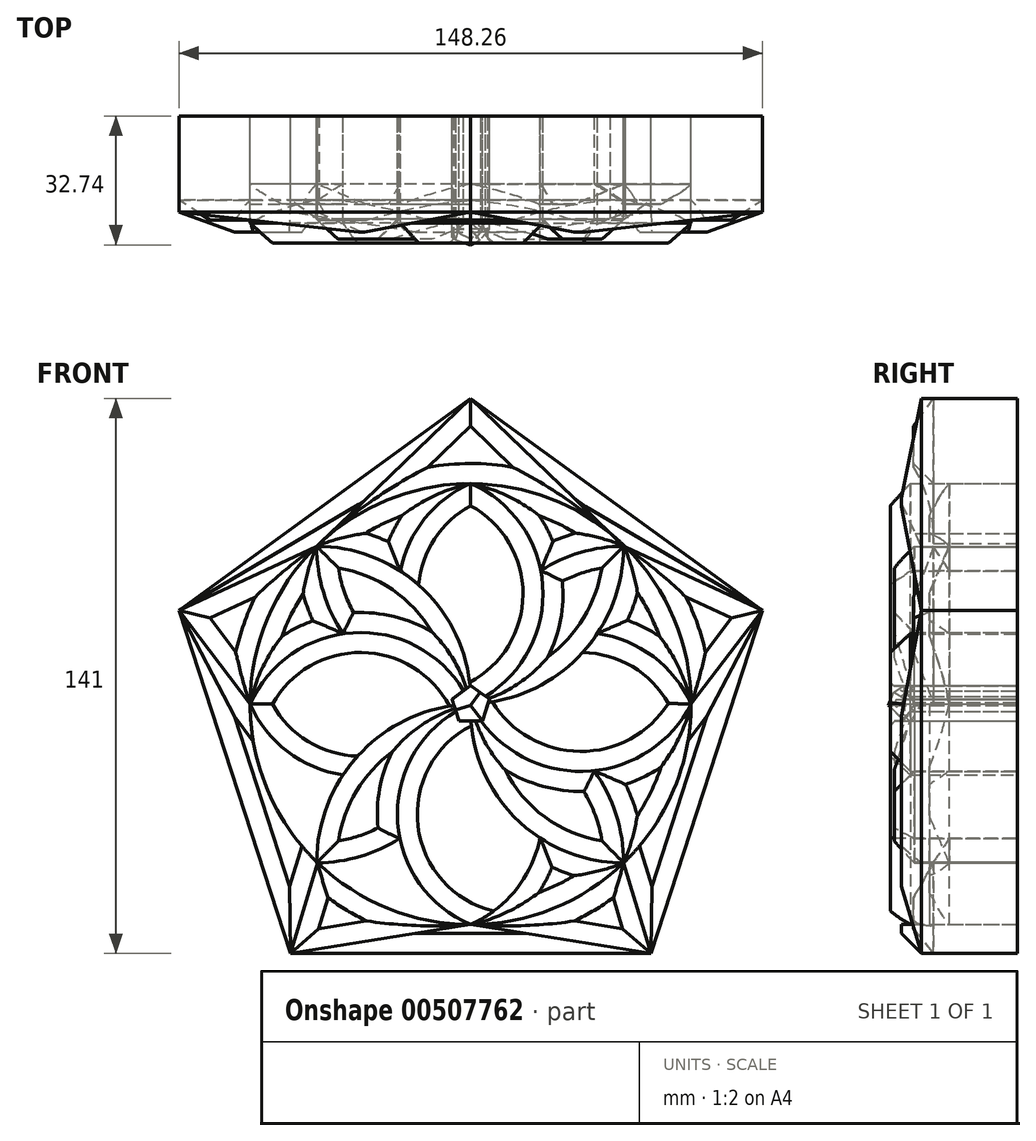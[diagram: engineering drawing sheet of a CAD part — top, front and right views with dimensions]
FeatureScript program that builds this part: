
annotation { "Feature Type Name" : "Feature", "Feature Type Description" : "" }
export const myFeature = defineFeature(function(context is Context, id is Id, definition is map)
    precondition{}
    {
        {
            var Q0;
            Q0=qCreatedBy(makeId("Front.planeOp"),FACE);
            var sketch = newSketch(context, id + "F0", { "sketchPlane" : qUnion([Q0])});
            skCircle(sketch, "E0", {"center": v(0, 0) * mm, "radius": 56.02 * mm});
            skLineSegment(sketch, "E1.top", {"start": v(-39.14, -40.34) * mm, "end": v(-38.88, -40.34) * mm});
            skArc(sketch, "E2", {"start": v(3.77, 1.96) * mm, "mid": v(18.3, 30.13) * mm, "end": v(0, 56.02) * mm});
            skArc(sketch, "E3", {"start": v(0, 56.02) * mm, "mid": v(-11.67, 47.1) * mm, "end": v(-17.83, 33.78) * mm});
            skArc(sketch, "E4", {"start": v(38.88, 40.08) * mm, "mid": v(27.9, 38.5) * mm, "end": v(17.8, 33.88) * mm});
            skArc(sketch, "E5", {"start": v(56.02, 0) * mm, "mid": v(46.42, 12.04) * mm, "end": v(32.18, 17.9) * mm});
            skArc(sketch, "E6", {"start": v(2.69, -4.33) * mm, "mid": v(30.56, -17.02) * mm, "end": v(56.02, 0) * mm});
            skArc(sketch, "E7", {"start": v(4.47, 0.39) * mm, "mid": v(29.08, 13.82) * mm, "end": v(38.88, 40.08) * mm});
            skArc(sketch, "E8", {"start": v(38.88, -40.34) * mm, "mid": v(36.96, -28.05) * mm, "end": v(31.4, -16.94) * mm});
            skArc(sketch, "E9", {"start": v(0.08, -4.34) * mm, "mid": v(12.42, -29.95) * mm, "end": v(38.88, -40.34) * mm});
            skArc(sketch, "E10", {"start": v(-39.14, 40.08) * mm, "mid": v(-37.42, 28.47) * mm, "end": v(-32.41, 17.86) * mm});
            skArc(sketch, "E11", {"start": v(-39.14, -40.34) * mm, "mid": v(-28.13, -38.76) * mm, "end": v(-18, -34.15) * mm});
            skArc(sketch, "E12", {"start": v(-4.22, -0.35) * mm, "mid": v(-29.18, -13.8) * mm, "end": v(-39.14, -40.34) * mm});
            skArc(sketch, "E13", {"start": v(0, -56.02) * mm, "mid": v(11.5, -47.18) * mm, "end": v(17.64, -34.03) * mm});
            skArc(sketch, "E14", {"start": v(-3.71, -1.86) * mm, "mid": v(-18.56, -30.09) * mm, "end": v(0, -56.02) * mm});
            skArc(sketch, "E15", {"start": v(-56.02, 0) * mm, "mid": v(-46.54, -12.06) * mm, "end": v(-32.4, -18) * mm});
            skArc(sketch, "E16", {"start": v(-1.77, 3.4) * mm, "mid": v(-29.92, 18.12) * mm, "end": v(-56.02, 0) * mm});
            skLineSegment(sketch, "E17.trimOffspring", {"start": v(-39.14, -40.08) * mm, "end": v(-39.14, -40.34) * mm});
            skArc(sketch, "E18.trimOffspring", {"start": v(0, -0.3) * mm, "mid": v(0, -0.15) * mm, "end": v(0, 0) * mm});
            skPoint(sketch, "E19.cCircle.perimeterSnap0", {"position": v(0.02, -1.3) * mm});
            skLineSegment(sketch, "E19.0", {"start": v(2.95, -4.33) * mm, "end": v(-2.91, -4.35) * mm});
            skLineSegment(sketch, "E19.1", {"start": v(-2.91, -4.35) * mm, "end": v(-4.74, 1.23) * mm});
            skLineSegment(sketch, "E19.2", {"start": v(-4.74, 1.23) * mm, "end": v(0, 4.68) * mm});
            skLineSegment(sketch, "E19.3", {"start": v(0, 4.68) * mm, "end": v(4.75, 1.25) * mm});
            skLineSegment(sketch, "E19.4", {"start": v(4.75, 1.25) * mm, "end": v(2.95, -4.33) * mm});
            skPoint(sketch, "E19.0.midPoint", {"position": v(0.02, -4.34) * mm});
            skPoint(sketch, "E19.0.midPoint.positionSnap0", {"position": v(0.02, -1.3) * mm});
            skArc(sketch, "E20.trimOffspring", {"start": v(-0.16, 4.57) * mm, "mid": v(-12.77, 29.87) * mm, "end": v(-39.14, 40.08) * mm});
            skArc(sketch, "E21.trimOffspring", {"start": v(-3.83, -1.56) * mm, "mid": v(-3.77, -1.71) * mm, "end": v(-3.71, -1.86) * mm, "construction": true});
            skArc(sketch, "E22.trimOffspring", {"start": v(0.02, -4.34) * mm, "mid": v(0.05, -4.34) * mm, "end": v(0.08, -4.34) * mm, "construction": true});
            skLineSegment(sketch, "E23.0", {"start": v(45.82, -63.36) * mm, "end": v(-45.8, -63.36) * mm});
            skLineSegment(sketch, "E23.1", {"start": v(-45.8, -63.36) * mm, "end": v(-74.12, 23.78) * mm});
            skLineSegment(sketch, "E23.2", {"start": v(-74.12, 23.78) * mm, "end": v(0, 77.64) * mm});
            skLineSegment(sketch, "E23.3", {"start": v(0, 77.64) * mm, "end": v(74.14, 23.78) * mm});
            skLineSegment(sketch, "E23.4", {"start": v(74.14, 23.78) * mm, "end": v(45.82, -63.36) * mm});
            skPoint(sketch, "E23.0.midPoint", {"position": v(0, -63.36) * mm});
            skLineSegment(sketch, "E24", {"start": v(-74.12, 23.78) * mm, "end": v(-56.02, 0) * mm});
            skLineSegment(sketch, "E25", {"start": v(-74.12, 23.78) * mm, "end": v(-39.14, 40.08) * mm});
            skLineSegment(sketch, "E26", {"start": v(0, 77.64) * mm, "end": v(-39.14, 40.08) * mm});
            skLineSegment(sketch, "E27", {"start": v(0, 77.64) * mm, "end": v(38.88, 40.08) * mm});
            skLineSegment(sketch, "E28", {"start": v(74.14, 23.78) * mm, "end": v(38.88, 40.08) * mm});
            skLineSegment(sketch, "E29", {"start": v(74.14, 23.78) * mm, "end": v(56.02, 0) * mm});
            skLineSegment(sketch, "E30", {"start": v(45.82, -63.36) * mm, "end": v(38.88, -40.34) * mm});
            skLineSegment(sketch, "E31", {"start": v(45.82, -63.36) * mm, "end": v(0, -56.02) * mm});
            skLineSegment(sketch, "E32", {"start": v(-45.8, -63.36) * mm, "end": v(-38.88, -40.34) * mm});
            skLineSegment(sketch, "E33", {"start": v(-45.8, -63.36) * mm, "end": v(0, -56.02) * mm});
            skSolve(sketch);
        }
        {
            var Q0;
            Q0=makeQuery(id+"F0.imprint","IMPRINT",FACE,{"disambiguationData":[TD([[makeQuery(id+"F0.imprint","IMPRINT",EDGE,{"derivedFrom":sQuery(id+"F0.wireOp",EDGE,"E1.top")}),-1.0]])]});
            var Q1;
            {var subQ4=sQuery(id+"F0.wireOp",EDGE,"E23.2");Q1=makeQuery(id+"F0.imprint","IMPRINT",FACE,{"disambiguationData":[TD([[makeQuery(id+"F0.imprint","IMPRINT",EDGE,{"derivedFrom":subQ4}),-1.0]])]});}
            var Q2;
            {var subQ5=sQuery(id+"F0.wireOp",EDGE,"E23.3");Q2=makeQuery(id+"F0.imprint","IMPRINT",FACE,{"disambiguationData":[TD([[makeQuery(id+"F0.imprint","IMPRINT",EDGE,{"derivedFrom":subQ5}),-1.0]])]});}
            var Q3;
            Q3=makeQuery(id+"F0.imprint","IMPRINT",FACE,{"disambiguationData":[TD([[makeQuery(id+"F0.imprint","IMPRINT",EDGE,{"derivedFrom":sQuery(id+"F0.wireOp",EDGE,"E23.0")}),-1.0]])]});
            var Q4;
            Q4=makeQuery(id+"F0.imprint","IMPRINT",FACE,{"disambiguationData":[TD([[makeQuery(id+"F0.imprint","IMPRINT",EDGE,{"derivedFrom":sQuery(id+"F0.wireOp",EDGE,"E23.4")}),-1.0]])]});
            extrude(context, id + "F1", {"entities" : qUnion([Q0, Q1, Q2, Q3, Q4]), "depth" : 29.46 * mm});
        }
        {
            var Q0;
            {var subQ0=sQuery(id+"F0.wireOp",EDGE,"E0");var subQ2=sQuery(id+"F0.wireOp",EDGE,"E27");var subQ3=makeQuery(id+"F0.imprint","INTERSECT",VERTEX,{"derivedFrom":[subQ0,subQ2]});Q0=makeQuery(id+"F0.imprint","IMPRINT",FACE,{"disambiguationData":[TD([[makeQuery(id+"F0.imprint","IMPRINT",EDGE,{"disambiguationData":[TD([[subQ3,-1.0]])],"derivedFrom":subQ0}),-1.0]])]});}
            var Q1;
            {var subQ2=sQuery(id+"F0.wireOp",EDGE,"E24");Q1=makeQuery(id+"F0.imprint","IMPRINT",FACE,{"disambiguationData":[TD([[makeQuery(id+"F0.imprint","IMPRINT",EDGE,{"derivedFrom":subQ2}),1.0]])]});}
            var Q2;
            {var subQ0=sQuery(id+"F0.wireOp",EDGE,"E32");Q2=makeQuery(id+"F0.imprint","IMPRINT",FACE,{"disambiguationData":[TD([[makeQuery(id+"F0.imprint","IMPRINT",EDGE,{"derivedFrom":subQ0}),-1.0]])]});}
            var Q3;
            {var subQ0=sQuery(id+"F0.wireOp",EDGE,"E30");Q3=makeQuery(id+"F0.imprint","IMPRINT",FACE,{"disambiguationData":[TD([[makeQuery(id+"F0.imprint","IMPRINT",EDGE,{"derivedFrom":subQ0}),1.0]])]});}
            var Q4;
            {var subQ0=sQuery(id+"F0.wireOp",EDGE,"E29");Q4=makeQuery(id+"F0.imprint","IMPRINT",FACE,{"disambiguationData":[TD([[makeQuery(id+"F0.imprint","IMPRINT",EDGE,{"derivedFrom":subQ0}),-1.0]])]});}
            extrude(context, id + "F2", {"entities" : qUnion([Q0, Q1, Q2, Q3, Q4]), "depth" : 26.42 * mm});
        }
        {
            var Q0;
            {var subQ0=sQuery(id+"F0.wireOp",EDGE,"E3");Q0=makeQuery(id+"F0.imprint","IMPRINT",FACE,{"disambiguationData":[TD([[makeQuery(id+"F0.imprint","IMPRINT",EDGE,{"derivedFrom":subQ0}),-1.0]])]});}
            var Q1;
            {var subQ0=sQuery(id+"F0.wireOp",EDGE,"E10");Q1=makeQuery(id+"F0.imprint","IMPRINT",FACE,{"disambiguationData":[TD([[makeQuery(id+"F0.imprint","IMPRINT",EDGE,{"derivedFrom":subQ0}),-1.0]])]});}
            var Q2;
            {var subQ0=sQuery(id+"F0.wireOp",EDGE,"E15");Q2=makeQuery(id+"F0.imprint","IMPRINT",FACE,{"disambiguationData":[TD([[makeQuery(id+"F0.imprint","IMPRINT",EDGE,{"derivedFrom":subQ0}),-1.0]])]});}
            var Q3;
            {var subQ2=sQuery(id+"F0.wireOp",EDGE,"E11");var subQ4=sQuery(id+"F0.wireOp",EDGE,"E14");var subQ5=makeQuery(id+"F0.imprint","INTERSECT",VERTEX,{"derivedFrom":[subQ2,subQ4]});Q3=makeQuery(id+"F0.imprint","IMPRINT",FACE,{"disambiguationData":[TD([[makeQuery(id+"F0.imprint","IMPRINT",EDGE,{"disambiguationData":[TD([[subQ5,1.0]])],"derivedFrom":subQ2}),-1.0]])]});}
            var Q4;
            {var subQ3=sQuery(id+"F0.wireOp",EDGE,"E13");Q4=makeQuery(id+"F0.imprint","IMPRINT",FACE,{"disambiguationData":[TD([[makeQuery(id+"F0.imprint","IMPRINT",EDGE,{"derivedFrom":subQ3}),-1.0]])]});}
            var Q5;
            {var subQ3=sQuery(id+"F0.wireOp",EDGE,"E8");Q5=makeQuery(id+"F0.imprint","IMPRINT",FACE,{"disambiguationData":[TD([[makeQuery(id+"F0.imprint","IMPRINT",EDGE,{"derivedFrom":subQ3}),-1.0]])]});}
            var Q6;
            {var subQ0=sQuery(id+"F0.wireOp",EDGE,"E5");Q6=makeQuery(id+"F0.imprint","IMPRINT",FACE,{"disambiguationData":[TD([[makeQuery(id+"F0.imprint","IMPRINT",EDGE,{"derivedFrom":subQ0}),-1.0]])]});}
            var Q7;
            {var subQ5=sQuery(id+"F0.wireOp",EDGE,"E4");Q7=makeQuery(id+"F0.imprint","IMPRINT",FACE,{"disambiguationData":[TD([[makeQuery(id+"F0.imprint","IMPRINT",EDGE,{"derivedFrom":subQ5}),-1.0]])]});}
            extrude(context, id + "F3", {"entities" : qUnion([Q0, Q1, Q2, Q3, Q4, Q5, Q6, Q7]), "depth" : 22.35 * mm});
        }
        {
            var Q0;
            {var subQ8=sQuery(id+"F0.wireOp",EDGE,"E3");Q0=makeQuery(id+"F0.imprint","IMPRINT",FACE,{"disambiguationData":[TD([[makeQuery(id+"F0.imprint","IMPRINT",EDGE,{"derivedFrom":subQ8}),1.0]])]});}
            var Q1;
            {var subQ4=sQuery(id+"F0.wireOp",EDGE,"E13");Q1=makeQuery(id+"F0.imprint","IMPRINT",FACE,{"disambiguationData":[TD([[makeQuery(id+"F0.imprint","IMPRINT",EDGE,{"derivedFrom":subQ4}),1.0]])]});}
            var Q2;
            {var subQ1=sQuery(id+"F0.wireOp",EDGE,"E5");Q2=makeQuery(id+"F0.imprint","IMPRINT",FACE,{"disambiguationData":[TD([[makeQuery(id+"F0.imprint","IMPRINT",EDGE,{"derivedFrom":subQ1}),1.0]])]});}
            var Q3;
            {var subQ2=sQuery(id+"F0.wireOp",EDGE,"E15");Q3=makeQuery(id+"F0.imprint","IMPRINT",FACE,{"disambiguationData":[TD([[makeQuery(id+"F0.imprint","IMPRINT",EDGE,{"derivedFrom":subQ2}),1.0]])]});}
            extrude(context, id + "F4", {"entities" : qUnion([Q0, Q1, Q2, Q3]), "depth" : 32.26 * mm});
        }
        {
            var Q0;
            {var subQ6=sQuery(id+"F0.wireOp",EDGE,"E10");Q0=makeQuery(id+"F0.imprint","IMPRINT",FACE,{"disambiguationData":[TD([[makeQuery(id+"F0.imprint","IMPRINT",EDGE,{"derivedFrom":subQ6}),1.0]])]});}
            var Q1;
            {var subQ0=sQuery(id+"F0.wireOp",EDGE,"E12");var subQ2=sQuery(id+"F0.wireOp",EDGE,"E0");var subQ3=makeQuery(id+"F0.imprint","INTERSECT",VERTEX,{"derivedFrom":[subQ2,subQ0]});Q1=makeQuery(id+"F0.imprint","IMPRINT",FACE,{"disambiguationData":[TD([[makeQuery(id+"F0.imprint","IMPRINT",EDGE,{"disambiguationData":[TD([[subQ3,-1.0]])],"derivedFrom":subQ2}),1.0]])]});}
            var Q2;
            {var subQ1=sQuery(id+"F0.wireOp",EDGE,"E8");Q2=makeQuery(id+"F0.imprint","IMPRINT",FACE,{"disambiguationData":[TD([[makeQuery(id+"F0.imprint","IMPRINT",EDGE,{"derivedFrom":subQ1}),1.0]])]});}
            var Q3;
            {var subQ4=sQuery(id+"F0.wireOp",EDGE,"E4");Q3=makeQuery(id+"F0.imprint","IMPRINT",FACE,{"disambiguationData":[TD([[makeQuery(id+"F0.imprint","IMPRINT",EDGE,{"derivedFrom":subQ4}),1.0]])]});}
            extrude(context, id + "F5", {"entities" : qUnion([Q0, Q1, Q2, Q3]), "depth" : 31.24 * mm});
        }
        {
            var Q0;
            {var subQ10=sQuery(id+"F0.wireOp",EDGE,"E19.0");var subQ11=makeQuery(id+"F0.imprint","INTERSECT",VERTEX,{"derivedFrom":[sQuery(id+"F0.wireOp",EDGE,"E6"),subQ10]});Q0=makeQuery(id+"F0.imprint","IMPRINT",FACE,{"disambiguationData":[TD([[makeQuery(id+"F0.imprint","IMPRINT",EDGE,{"disambiguationData":[TD([[subQ11,1.0]])],"derivedFrom":subQ10}),-1.0]])]});}
            extrude(context, id + "F6", {"entities" : qUnion([Q0]), "depth" : 33.78 * mm});
        }
        {
            var Q0;
            Q0=makeQuery(id+"F1.opExtrude","CAP_EDGE",EDGE,{"disambiguationData":[OSD([sQuery(id+"F0.wireOp",EDGE,"E23.3")])],"isStart":false});
            var Q1;
            Q1=makeQuery(id+"F1.opExtrude","CAP_EDGE",EDGE,{"disambiguationData":[OSD([sQuery(id+"F0.wireOp",EDGE,"E23.0")])],"isStart":false});
            var Q2;
            Q2=makeQuery(id+"F1.opExtrude","CAP_EDGE",EDGE,{"disambiguationData":[OSD([sQuery(id+"F0.wireOp",EDGE,"E23.4")])],"isStart":false});
            var Q3;
            Q3=makeQuery(id+"F1.opExtrude","CAP_EDGE",EDGE,{"disambiguationData":[OSD([sQuery(id+"F0.wireOp",EDGE,"E23.1")])],"isStart":false});
            var Q4;
            Q4=makeQuery(id+"F1.opExtrude","CAP_EDGE",EDGE,{"disambiguationData":[OSD([sQuery(id+"F0.wireOp",EDGE,"E32")])],"isStart":false});
            var Q5;
            Q5=makeQuery(id+"F1.opExtrude","CAP_EDGE",EDGE,{"disambiguationData":[OSD([sQuery(id+"F0.wireOp",EDGE,"E24")])],"isStart":false});
            var Q6;
            Q6=makeQuery(id+"F1.opExtrude","CAP_EDGE",EDGE,{"disambiguationData":[OSD([sQuery(id+"F0.wireOp",EDGE,"E23.2")])],"isStart":false});
            var Q7;
            Q7=makeQuery(id+"F1.opExtrude","CAP_EDGE",EDGE,{"disambiguationData":[OSD([sQuery(id+"F0.wireOp",EDGE,"E25")])],"isStart":false});
            var Q8;
            Q8=makeQuery(id+"F1.opExtrude","CAP_EDGE",EDGE,{"disambiguationData":[OSD([sQuery(id+"F0.wireOp",EDGE,"E30")])],"isStart":false});
            var Q9;
            Q9=makeQuery(id+"F1.opExtrude","CAP_EDGE",EDGE,{"disambiguationData":[OSD([sQuery(id+"F0.wireOp",EDGE,"E29")])],"isStart":false});
            var Q10;
            Q10=makeQuery(id+"F1.opExtrude","CAP_EDGE",EDGE,{"disambiguationData":[OSD([sQuery(id+"F0.wireOp",EDGE,"E28")])],"isStart":false});
            chamfer(context, id + "F7", {"entities" : qUnion([Q0, Q1, Q2, Q3, Q4, Q5, Q6, Q7, Q8, Q9, Q10]), "width" : 5.08 * mm, "tangentPropagation" : true});
        }
        {
            var Q0;
            Q0=makeQuery(id+"F2.opExtrude","CAP_FACE",FACE,{"disambiguationData":[OSD([sQuery(id+"F0.wireOp",EDGE,"E0"),sQuery(id+"F0.wireOp",EDGE,"E24"),sQuery(id+"F0.wireOp",EDGE,"E25")])],"isStart":false});
            var Q1;
            Q1=makeQuery(id+"F2.opExtrude","CAP_FACE",FACE,{"disambiguationData":[OSD([sQuery(id+"F0.wireOp",EDGE,"E0"),sQuery(id+"F0.wireOp",EDGE,"E26"),sQuery(id+"F0.wireOp",EDGE,"E27")])],"isStart":false});
            var Q2;
            Q2=makeQuery(id+"F2.opExtrude","CAP_FACE",FACE,{"disambiguationData":[OSD([sQuery(id+"F0.wireOp",EDGE,"E0"),sQuery(id+"F0.wireOp",EDGE,"E28"),sQuery(id+"F0.wireOp",EDGE,"E29")])],"isStart":false});
            var Q3;
            Q3=makeQuery(id+"F2.opExtrude","CAP_FACE",FACE,{"disambiguationData":[OSD([sQuery(id+"F0.wireOp",EDGE,"E0"),sQuery(id+"F0.wireOp",EDGE,"E30"),sQuery(id+"F0.wireOp",EDGE,"E31")])],"isStart":false});
            var Q4;
            Q4=makeQuery(id+"F2.opExtrude","CAP_FACE",FACE,{"disambiguationData":[OSD([sQuery(id+"F0.wireOp",EDGE,"E0"),sQuery(id+"F0.wireOp",EDGE,"E32"),sQuery(id+"F0.wireOp",EDGE,"E33")])],"isStart":false});
            var Q5;
            Q5=makeQuery(id+"F5.opExtrude","CAP_FACE",FACE,{"disambiguationData":[OSD([sQuery(id+"F0.wireOp",EDGE,"E10"),sQuery(id+"F0.wireOp",EDGE,"E16"),sQuery(id+"F0.wireOp",EDGE,"E19.2"),sQuery(id+"F0.wireOp",EDGE,"E20.trimOffspring")])],"isStart":false});
            var Q6;
            Q6=makeQuery(id+"F5.opExtrude","CAP_FACE",FACE,{"disambiguationData":[OSD([sQuery(id+"F0.wireOp",EDGE,"E2"),sQuery(id+"F0.wireOp",EDGE,"E4"),sQuery(id+"F0.wireOp",EDGE,"E7"),sQuery(id+"F0.wireOp",EDGE,"E19.3"),sQuery(id+"F0.wireOp",EDGE,"E19.4")])],"isStart":false});
            var Q7;
            Q7=makeQuery(id+"F5.opExtrude","CAP_FACE",FACE,{"disambiguationData":[OSD([sQuery(id+"F0.wireOp",EDGE,"E6"),sQuery(id+"F0.wireOp",EDGE,"E8"),sQuery(id+"F0.wireOp",EDGE,"E9"),sQuery(id+"F0.wireOp",EDGE,"E19.0")])],"isStart":false});
            var Q8;
            Q8=makeQuery(id+"F5.opExtrude","CAP_FACE",FACE,{"disambiguationData":[OSD([sQuery(id+"F0.wireOp",EDGE,"E0"),sQuery(id+"F0.wireOp",EDGE,"E11"),sQuery(id+"F0.wireOp",EDGE,"E12"),sQuery(id+"F0.wireOp",EDGE,"E14"),sQuery(id+"F0.wireOp",EDGE,"E19.1")])],"isStart":false});
            chamfer(context, id + "F8", {"entities" : qUnion([Q0, Q1, Q2, Q3, Q4, Q5, Q6, Q7, Q8]), "width" : 5.08 * mm, "tangentPropagation" : true});
        }
        {
            var Q0;
            Q0=makeQuery(id+"F3.opExtrude","CAP_FACE",FACE,{"disambiguationData":[OSD([sQuery(id+"F0.wireOp",EDGE,"E0"),sQuery(id+"F0.wireOp",EDGE,"E11"),sQuery(id+"F0.wireOp",EDGE,"E14")])],"isStart":false});
            var Q1;
            Q1=makeQuery(id+"F4.opExtrude","CAP_EDGE",EDGE,{"disambiguationData":[OSD([sQuery(id+"F0.wireOp",EDGE,"E15")])],"isStart":false});
            var Q2;
            Q2=makeQuery(id+"F3.opExtrude","CAP_FACE",FACE,{"disambiguationData":[OSD([sQuery(id+"F0.wireOp",EDGE,"E0"),sQuery(id+"F0.wireOp",EDGE,"E10"),sQuery(id+"F0.wireOp",EDGE,"E16")])],"isStart":false});
            var Q3;
            Q3=makeQuery(id+"F3.opExtrude","CAP_FACE",FACE,{"disambiguationData":[OSD([sQuery(id+"F0.wireOp",EDGE,"E0"),sQuery(id+"F0.wireOp",EDGE,"E3"),sQuery(id+"F0.wireOp",EDGE,"E20.trimOffspring"),sQuery(id+"F0.wireOp",EDGE,"E26")])],"isStart":false});
            var Q4;
            Q4=makeQuery(id+"F3.opExtrude","CAP_FACE",FACE,{"disambiguationData":[OSD([sQuery(id+"F0.wireOp",EDGE,"E0"),sQuery(id+"F0.wireOp",EDGE,"E2"),sQuery(id+"F0.wireOp",EDGE,"E4"),sQuery(id+"F0.wireOp",EDGE,"E27")])],"isStart":false});
            var Q5;
            Q5=makeQuery(id+"F3.opExtrude","CAP_FACE",FACE,{"disambiguationData":[OSD([sQuery(id+"F0.wireOp",EDGE,"E0"),sQuery(id+"F0.wireOp",EDGE,"E5"),sQuery(id+"F0.wireOp",EDGE,"E7"),sQuery(id+"F0.wireOp",EDGE,"E28")])],"isStart":false});
            var Q6;
            Q6=makeQuery(id+"F3.opExtrude","CAP_FACE",FACE,{"disambiguationData":[OSD([sQuery(id+"F0.wireOp",EDGE,"E0"),sQuery(id+"F0.wireOp",EDGE,"E6"),sQuery(id+"F0.wireOp",EDGE,"E8")])],"isStart":false});
            var Q7;
            Q7=makeQuery(id+"F3.opExtrude","CAP_FACE",FACE,{"disambiguationData":[OSD([sQuery(id+"F0.wireOp",EDGE,"E0"),sQuery(id+"F0.wireOp",EDGE,"E9"),sQuery(id+"F0.wireOp",EDGE,"E13")])],"isStart":false});
            var Q8;
            Q8=makeQuery(id+"F3.opExtrude","CAP_FACE",FACE,{"disambiguationData":[OSD([sQuery(id+"F0.wireOp",EDGE,"E0"),sQuery(id+"F0.wireOp",EDGE,"E12"),sQuery(id+"F0.wireOp",EDGE,"E15")])],"isStart":false});
            chamfer(context, id + "F9", {"entities" : qUnion([Q0, Q1, Q2, Q3, Q4, Q5, Q6, Q7, Q8]), "width" : 5.08 * mm, "tangentPropagation" : true});
        }
        {
            var Q0;
            Q0=makeQuery(id+"F4.opExtrude","CAP_EDGE",EDGE,{"disambiguationData":[OSD([sQuery(id+"F0.wireOp",EDGE,"E16")])],"isStart":false});
            var Q1;
            Q1=makeQuery(id+"F4.opExtrude","CAP_EDGE",EDGE,{"disambiguationData":[OSD([sQuery(id+"F0.wireOp",EDGE,"E14")])],"isStart":false});
            var Q2;
            Q2=makeQuery(id+"F4.opExtrude","CAP_EDGE",EDGE,{"disambiguationData":[OSD([sQuery(id+"F0.wireOp",EDGE,"E6")])],"isStart":false});
            var Q3;
            Q3=makeQuery(id+"F4.opExtrude","CAP_EDGE",EDGE,{"disambiguationData":[OSD([sQuery(id+"F0.wireOp",EDGE,"E5")])],"isStart":false});
            var Q4;
            Q4=makeQuery(id+"F4.opExtrude","CAP_EDGE",EDGE,{"disambiguationData":[OSD([sQuery(id+"F0.wireOp",EDGE,"E2")])],"isStart":false});
            var Q5;
            Q5=makeQuery(id+"F4.opExtrude","CAP_EDGE",EDGE,{"disambiguationData":[OSD([sQuery(id+"F0.wireOp",EDGE,"E3")])],"isStart":false});
            var Q6;
            Q6=makeQuery(id+"F6.opExtrude","CAP_EDGE",EDGE,{"disambiguationData":[OSD([sQuery(id+"F0.wireOp",EDGE,"E19.0")])],"isStart":false});
            var Q7;
            Q7=makeQuery(id+"F6.opExtrude","CAP_EDGE",EDGE,{"disambiguationData":[OSD([sQuery(id+"F0.wireOp",EDGE,"E19.4")])],"isStart":false});
            var Q8;
            Q8=makeQuery(id+"F6.opExtrude","CAP_EDGE",EDGE,{"disambiguationData":[OSD([sQuery(id+"F0.wireOp",EDGE,"E19.2")])],"isStart":false});
            chamfer(context, id + "F10", {"entities" : qUnion([Q0, Q1, Q2, Q3, Q4, Q5, Q6, Q7, Q8]), "width" : 5.08 * mm, "tangentPropagation" : true});
        }
    });
